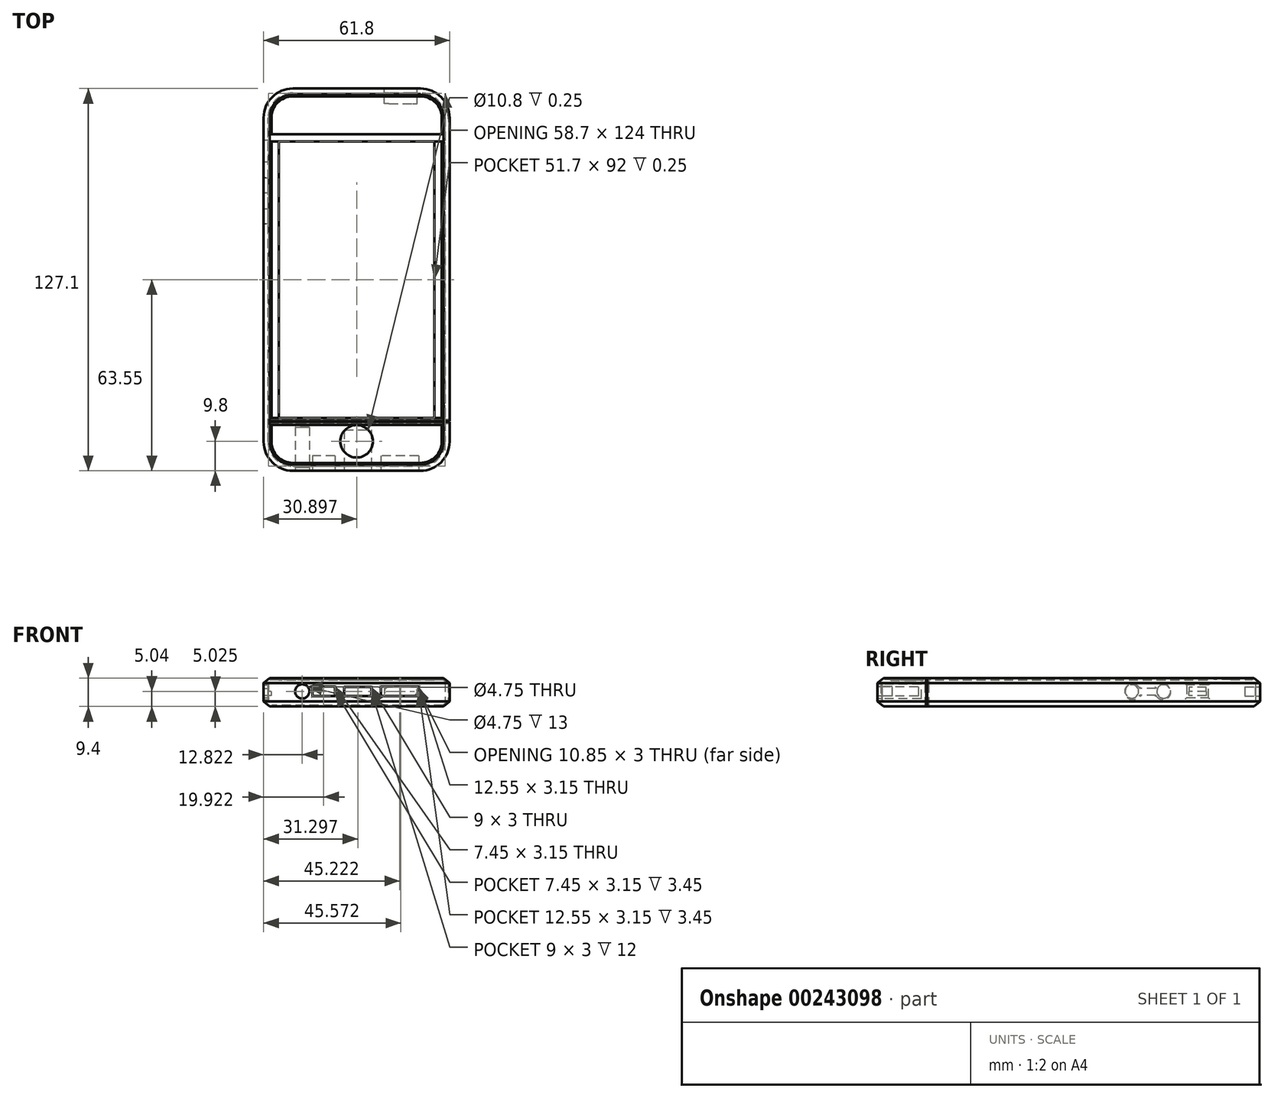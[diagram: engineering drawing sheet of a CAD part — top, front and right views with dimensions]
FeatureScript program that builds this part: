
annotation { "Feature Type Name" : "Feature", "Feature Type Description" : "" }
export const myFeature = defineFeature(function(context is Context, id is Id, definition is map)
    precondition{}
    {
        {
            var Q0;
            Q0=qCreatedBy(makeId("Top.planeOp"),FACE);
            var sketch = newSketch(context, id + "F0", { "sketchPlane" : qUnion([Q0])});
            skLineSegment(sketch, "E0.bottom", {"start": v(30.56, 124) * mm, "end": v(89.26, 124) * mm});
            skLineSegment(sketch, "E0.top", {"start": v(30.56, 0) * mm, "end": v(89.26, 0) * mm});
            skLineSegment(sketch, "E0.left", {"start": v(30.56, 124) * mm, "end": v(30.56, 0) * mm});
            skLineSegment(sketch, "E0.right", {"start": v(89.26, 124) * mm, "end": v(89.26, 0) * mm});
            skSolve(sketch);
        }
        {
            var Q0;
            Q0=makeQuery(id+"F0.imprint","IMPRINT",FACE,{"disambiguationData":[TD([[makeQuery(id+"F0.imprint","IMPRINT",EDGE,{"derivedFrom":sQuery(id+"F0.wireOp",EDGE,"E0.bottom")}),-1.0]])]});
            extrude(context, id + "F1", {"entities" : qUnion([Q0]), "depth" : 7.75 * mm});
        }
        {
            var Q0;
            Q0=makeQuery(id+"F1.opExtrude","CAP_FACE",FACE,{"disambiguationData":[OSD([sQuery(id+"F0.wireOp",EDGE,"E0.bottom"),sQuery(id+"F0.wireOp",EDGE,"E0.top"),sQuery(id+"F0.wireOp",EDGE,"E0.left"),sQuery(id+"F0.wireOp",EDGE,"E0.right")])],"isStart":false});
            var sketch = newSketch(context, id + "F2", { "sketchPlane" : qUnion([Q0])});
            skLineSegment(sketch, "E1", {"start": v(30.56, 0) * mm, "end": v(30.56, 16) * mm, "construction": true});
            skLineSegment(sketch, "E2", {"start": v(30.56, 124) * mm, "end": v(30.56, 108) * mm, "construction": true});
            skLineSegment(sketch, "E3", {"start": v(89.26, 124) * mm, "end": v(80.16, 124) * mm, "construction": true});
            skLineSegment(sketch, "E4", {"start": v(80.16, 124) * mm, "end": v(70.66, 124) * mm});
            skPoint(sketch, "E5", {"position": v(30.56, 113.5) * mm});
            skPoint(sketch, "E5.positionSnap0", {"position": v(30.56, 116) * mm});
            skLineSegment(sketch, "E6", {"start": v(89.26, 0) * mm, "end": v(89.26, 13.65) * mm, "construction": true});
            skCircle(sketch, "E7", {"center": v(59.9, 8.25) * mm, "radius": 5.4 * mm});
            skLineSegment(sketch, "E8", {"start": v(85.76, 16) * mm, "end": v(34.06, 16) * mm});
            skLineSegment(sketch, "E9", {"start": v(34.06, 16) * mm, "end": v(34.06, 108) * mm});
            skLineSegment(sketch, "E10", {"start": v(34.06, 108) * mm, "end": v(85.76, 108) * mm});
            skLineSegment(sketch, "E11", {"start": v(85.76, 108) * mm, "end": v(85.76, 16) * mm});
            skSolve(sketch);
        }
        {
            var Q0;
            Q0=makeQuery(id+"F1.opExtrude","CAP_FACE",FACE,{"disambiguationData":[OSD([sQuery(id+"F0.wireOp",EDGE,"E0.bottom"),sQuery(id+"F0.wireOp",EDGE,"E0.top"),sQuery(id+"F0.wireOp",EDGE,"E0.left"),sQuery(id+"F0.wireOp",EDGE,"E0.right")])],"isStart":true});
            var sketch = newSketch(context, id + "F3", { "sketchPlane" : qUnion([Q0])});
            skLineSegment(sketch, "E12", {"start": v(89.26, -124) * mm, "end": v(77.86, -124) * mm, "construction": true});
            skLineSegment(sketch, "E13", {"start": v(89.26, 0) * mm, "end": v(89.26, -10.45) * mm, "construction": true});
            skLineSegment(sketch, "E14", {"start": v(89.26, -10.45) * mm, "end": v(30.56, -10.45) * mm});
            skCircle(sketch, "E15", {"center": v(82.26, -116.6) * mm, "radius": 3.1 * mm});
            skCircle(sketch, "E16", {"center": v(72.23, -116.6) * mm, "radius": 1.93 * mm});
            skSolve(sketch);
        }
        {
            var Q0;
            Q0=makeQuery(id+"F1.opExtrude","SWEPT_FACE",FACE,{"disambiguationData":[OSD([sQuery(id+"F0.wireOp",EDGE,"E0.left")])]});
            var sketch = newSketch(context, id + "F4", { "sketchPlane" : qUnion([Q0])});
            skLineSegment(sketch, "E17", {"start": v(-124, 7.75) * mm, "end": v(-107.5, 7.75) * mm, "construction": true});
            skLineSegment(sketch, "E18", {"start": v(-107.5, 7.75) * mm, "end": v(-91.25, 7.75) * mm, "construction": true});
            skLineSegment(sketch, "E19", {"start": v(-91.25, 7.75) * mm, "end": v(-91.25, 0) * mm});
            skLineSegment(sketch, "E20", {"start": v(-91.25, 3.88) * mm, "end": v(-93.52, 3.88) * mm});
            skCircle(sketch, "E21", {"center": v(-93.52, 3.88) * mm, "radius": 2.27 * mm});
            skLineSegment(sketch, "E22", {"start": v(-91.25, 3.88) * mm, "end": v(-85.25, 3.88) * mm});
            skLineSegment(sketch, "E23", {"start": v(-85.25, 3.88) * mm, "end": v(-82.97, 3.88) * mm});
            skCircle(sketch, "E24", {"center": v(-82.97, 3.88) * mm, "radius": 2.27 * mm});
            skLineSegment(sketch, "E25", {"start": v(-93.52, 3.88) * mm, "end": v(-95.8, 3.88) * mm, "construction": true});
            skPoint(sketch, "E26.0", {"position": v(-124, 7.75) * mm});
            skLineSegment(sketch, "E27", {"start": v(-124, 7.75) * mm, "end": v(-101.9, 7.75) * mm, "construction": true});
            skLineSegment(sketch, "E28", {"start": v(-124, 0) * mm, "end": v(-107.7, 0) * mm, "construction": true});
            skLineSegment(sketch, "E29", {"start": v(-107.7, 3.88) * mm, "end": v(-107.7, 2.52) * mm});
            skLineSegment(sketch, "E30", {"start": v(-107.7, 2.52) * mm, "end": v(-101.9, 2.52) * mm});
            skLineSegment(sketch, "E31", {"start": v(-101.9, 2.52) * mm, "end": v(-101.9, 3.88) * mm});
            skLineSegment(sketch, "E32", {"start": v(-101.9, 3.88) * mm, "end": v(-101.9, 5.22) * mm});
            skLineSegment(sketch, "E33", {"start": v(-101.9, 5.22) * mm, "end": v(-107.7, 5.22) * mm});
            skLineSegment(sketch, "E34", {"start": v(-107.7, 5.22) * mm, "end": v(-107.7, 3.88) * mm});
            skLineSegment(sketch, "E35", {"start": v(-101.9, 3.88) * mm, "end": v(-107.7, 3.88) * mm});
            skSolve(sketch);
        }
        {
            var Q0;
            Q0=makeQuery(id+"F1.opExtrude","SWEPT_FACE",FACE,{"disambiguationData":[OSD([sQuery(id+"F0.wireOp",EDGE,"E0.top")])]});
            var sketch = newSketch(context, id + "F5", { "sketchPlane" : qUnion([Q0])});
            skLineSegment(sketch, "E36", {"start": v(89.26, 7.75) * mm, "end": v(80.5, 7.75) * mm, "construction": true});
            skLineSegment(sketch, "E37", {"start": v(80.5, 7.75) * mm, "end": v(67.96, 7.75) * mm, "construction": true});
            skLineSegment(sketch, "E38", {"start": v(89.26, 3.88) * mm, "end": v(30.56, 3.88) * mm, "construction": true});
            skLineSegment(sketch, "E39", {"start": v(80.5, 3.88) * mm, "end": v(80.5, 5.45) * mm});
            skLineSegment(sketch, "E40", {"start": v(80.5, 3.88) * mm, "end": v(80.5, 2.3) * mm});
            skLineSegment(sketch, "E41", {"start": v(80.5, 5.45) * mm, "end": v(67.96, 5.45) * mm});
            skLineSegment(sketch, "E42", {"start": v(67.96, 5.45) * mm, "end": v(67.96, 2.3) * mm});
            skLineSegment(sketch, "E43", {"start": v(67.96, 2.3) * mm, "end": v(80.5, 2.3) * mm});
            skLineSegment(sketch, "E44", {"start": v(67.96, 7.75) * mm, "end": v(64.8, 7.75) * mm, "construction": true});
            skLineSegment(sketch, "E45", {"start": v(64.8, 7.75) * mm, "end": v(55.8, 7.75) * mm, "construction": true});
            skLineSegment(sketch, "E46", {"start": v(55.8, 7.75) * mm, "end": v(52.66, 7.75) * mm, "construction": true});
            skLineSegment(sketch, "E47", {"start": v(52.66, 7.75) * mm, "end": v(45.2, 7.75) * mm, "construction": true});
            skLineSegment(sketch, "E48", {"start": v(52.66, 3.88) * mm, "end": v(52.66, 2.3) * mm, "construction": true});
            skLineSegment(sketch, "E49", {"start": v(52.66, 2.3) * mm, "end": v(45.2, 2.3) * mm});
            skLineSegment(sketch, "E50", {"start": v(45.2, 2.3) * mm, "end": v(45.2, 5.45) * mm});
            skLineSegment(sketch, "E51", {"start": v(45.2, 5.45) * mm, "end": v(52.66, 5.45) * mm});
            skLineSegment(sketch, "E52", {"start": v(52.66, 5.45) * mm, "end": v(52.66, 2.3) * mm});
            skLineSegment(sketch, "E53", {"start": v(55.8, 5.39) * mm, "end": v(64.8, 5.39) * mm});
            skLineSegment(sketch, "E54", {"start": v(64.8, 5.39) * mm, "end": v(64.8, 2.39) * mm});
            skLineSegment(sketch, "E55", {"start": v(64.8, 2.39) * mm, "end": v(55.8, 2.39) * mm});
            skLineSegment(sketch, "E56", {"start": v(55.8, 5.39) * mm, "end": v(55.8, 2.39) * mm});
            skPoint(sketch, "E57.endSnap0", {"position": v(41.83, 5.45) * mm});
            skCircle(sketch, "E58", {"center": v(41.83, 3.88) * mm, "radius": 2.37 * mm});
            skSolve(sketch);
        }
        {
            var Q0;
            Q0=makeQuery(id+"F1.opExtrude","SWEPT_EDGE",EDGE,{"disambiguationData":[OSD([sQuery(id+"F0.wireOp",EDGE,"E0.bottom"),sQuery(id+"F0.wireOp",EDGE,"E0.left")])]});
            var Q1;
            Q1=makeQuery(id+"F1.opExtrude","SWEPT_EDGE",EDGE,{"disambiguationData":[OSD([sQuery(id+"F0.wireOp",EDGE,"E0.bottom"),sQuery(id+"F0.wireOp",EDGE,"E0.right")])]});
            var Q2;
            Q2=makeQuery(id+"F1.opExtrude","SWEPT_EDGE",EDGE,{"disambiguationData":[OSD([sQuery(id+"F0.wireOp",EDGE,"E0.top"),sQuery(id+"F0.wireOp",EDGE,"E0.left")])]});
            var Q3;
            Q3=makeQuery(id+"F1.opExtrude","SWEPT_EDGE",EDGE,{"disambiguationData":[OSD([sQuery(id+"F0.wireOp",EDGE,"E0.top"),sQuery(id+"F0.wireOp",EDGE,"E0.right")])]});
            fillet(context, id + "F6", {"entities" : qUnion([Q0, Q1, Q2, Q3]), "radius" : 8.15 * mm, "tangentPropagation" : true, "allowEdgeOverflow" : false});
        }
        {
            var Q0;
            Q0=makeQuery(id+"F1.opExtrude","SWEPT_FACE",FACE,{"disambiguationData":[OSD([sQuery(id+"F0.wireOp",EDGE,"E0.bottom")])]});
            var sketch = newSketch(context, id + "F7", { "sketchPlane" : qUnion([Q0])});
            skLineSegment(sketch, "E59", {"start": v(-70.66, 0) * mm, "end": v(-80.16, 0) * mm, "construction": true});
            skArc(sketch, "E60", {"start": v(-78.5, 4.97) * mm, "mid": v(-79.6, 3.88) * mm, "end": v(-78.5, 2.78) * mm});
            skLineSegment(sketch, "E61", {"start": v(-78.5, 4.97) * mm, "end": v(-70.66, 4.98) * mm});
            skLineSegment(sketch, "E62", {"start": v(-70.66, 2.78) * mm, "end": v(-78.5, 2.78) * mm});
            skPoint(sketch, "E63.endSnap0", {"position": v(-70.66, 3.88) * mm});
            skArc(sketch, "E64", {"start": v(-70.66, 2.78) * mm, "mid": v(-69.56, 3.88) * mm, "end": v(-70.66, 4.98) * mm});
            skSolve(sketch);
        }
        {
            var Q0;
            Q0=makeQuery(id+"F5.imprint","IMPRINT",FACE,{"disambiguationData":[TD([[makeQuery(id+"F5.imprint","IMPRINT",EDGE,{"derivedFrom":sQuery(id+"F5.wireOp",EDGE,"E58")}),1.0]])]});
            extrude(context, id + "F8", {"entities" : qUnion([Q0]), "operationType" : NewBodyOperationType.REMOVE, "oppositeDirection" : true, "depth" : 13 * mm});
        }
        {
            var Q0;
            Q0=qSketchRegion(id+"F7",true);
            extrude(context, id + "F9", {"entities" : qUnion([Q0]), "operationType" : NewBodyOperationType.ADD, "depth" : .9 * mm});
        }
        {
            var Q0;
            Q0=makeQuery(id+"F4.imprint","IMPRINT",FACE,{"disambiguationData":[TD([[makeQuery(id+"F4.imprint","IMPRINT",EDGE,{"derivedFrom":sQuery(id+"F4.wireOp",EDGE,"E21")}),1.0]])]});
            var Q1;
            Q1=makeQuery(id+"F4.imprint","IMPRINT",FACE,{"disambiguationData":[TD([[makeQuery(id+"F4.imprint","IMPRINT",EDGE,{"derivedFrom":sQuery(id+"F4.wireOp",EDGE,"E24")}),1.0]])]});
            var Q2;
            Q2=makeQuery(id+"F4.imprint","IMPRINT",FACE,{"disambiguationData":[TD([[makeQuery(id+"F4.imprint","IMPRINT",EDGE,{"derivedFrom":sQuery(id+"F4.wireOp",EDGE,"E32")}),1.0]])]});
            extrude(context, id + "F10", {"entities" : qUnion([Q0, Q1, Q2]), "operationType" : NewBodyOperationType.ADD, "depth" : .9 * mm});
        }
        {
            var Q0;
            Q0=makeQuery(id+"F4.imprint","IMPRINT",FACE,{"disambiguationData":[TD([[makeQuery(id+"F4.imprint","IMPRINT",EDGE,{"derivedFrom":sQuery(id+"F4.wireOp",EDGE,"E29")}),1.0]])]});
            extrude(context, id + "F11", {"entities" : qUnion([Q0]), "operationType" : NewBodyOperationType.REMOVE, "oppositeDirection" : true, "depth" : .9 * mm});
        }
        {
            var Q0;
            Q0=makeQuery(id+"F5.imprint","IMPRINT",FACE,{"disambiguationData":[TD([[makeQuery(id+"F5.imprint","IMPRINT",EDGE,{"derivedFrom":sQuery(id+"F5.wireOp",EDGE,"E53")}),-1.0]])]});
            extrude(context, id + "F12", {"entities" : qUnion([Q0]), "operationType" : NewBodyOperationType.REMOVE, "oppositeDirection" : true, "depth" : 12 * mm});
        }
        {
            var Q0;
            Q0=makeQuery(id+"F2.imprint","IMPRINT",FACE,{"disambiguationData":[TD([[makeQuery(id+"F2.imprint","IMPRINT",EDGE,{"derivedFrom":sQuery(id+"F2.wireOp",EDGE,"E7")}),1.0]])]});
            var Q1;
            Q1=sQuery(id+"F2.wireOp",EDGE,"E7");
            extrude(context, id + "F13", {"entities" : qUnion([Q0]), "operationType" : NewBodyOperationType.REMOVE, "surfaceEntities" : qUnion([Q1]), "oppositeDirection" : true, "depth" : .25 * mm});
        }
        {
            var Q0;
            {var subQ2=sQuery(id+"F2.wireOp",EDGE,"E4");Q0=makeQuery(id+"F2.imprint","IMPRINT",FACE,{"disambiguationData":[TD([[makeQuery(id+"F2.imprint","IMPRINT",EDGE,{"derivedFrom":subQ2}),-1.0]])]});}
            var sketch = newSketch(context, id + "F14", { "sketchPlane" : qUnion([Q0])});
            skArc(sketch, "E65.0", {"start": v(81.1, 0) * mm, "mid": v(86.87, 2.39) * mm, "end": v(89.26, 8.15) * mm});
            skLineSegment(sketch, "E66.0", {"start": v(89.26, 115.85) * mm, "end": v(89.26, 8.15) * mm});
            skLineSegment(sketch, "E67.0", {"start": v(38.7, 0) * mm, "end": v(81.1, 0) * mm});
            skArc(sketch, "E68.0", {"start": v(30.56, 8.15) * mm, "mid": v(32.94, 2.39) * mm, "end": v(38.7, 0) * mm});
            skLineSegment(sketch, "E69.0", {"start": v(30.56, 115.85) * mm, "end": v(30.56, 8.15) * mm});
            skArc(sketch, "E70.0", {"start": v(38.7, 124) * mm, "mid": v(32.94, 121.61) * mm, "end": v(30.56, 115.85) * mm});
            skLineSegment(sketch, "E71.0", {"start": v(38.7, 124) * mm, "end": v(81.1, 124) * mm});
            skArc(sketch, "E72.0", {"start": v(89.26, 115.85) * mm, "mid": v(86.87, 121.61) * mm, "end": v(81.1, 124) * mm});
            skArc(sketch, "E73", {"start": v(88.2, 8.15) * mm, "mid": v(86.13, 3.13) * mm, "end": v(81.1, 1.05) * mm});
            skLineSegment(sketch, "E74", {"start": v(81.1, 1.05) * mm, "end": v(38.7, 1.05) * mm});
            skArc(sketch, "E75", {"start": v(31.6, 8.15) * mm, "mid": v(33.69, 3.13) * mm, "end": v(38.7, 1.05) * mm});
            skLineSegment(sketch, "E76", {"start": v(31.6, 8.15) * mm, "end": v(31.6, 115.85) * mm});
            skArc(sketch, "E77", {"start": v(31.6, 115.85) * mm, "mid": v(33.69, 120.87) * mm, "end": v(38.7, 122.95) * mm});
            skLineSegment(sketch, "E78", {"start": v(38.7, 122.95) * mm, "end": v(81.1, 122.95) * mm});
            skArc(sketch, "E79", {"start": v(81.1, 122.95) * mm, "mid": v(86.13, 120.87) * mm, "end": v(88.2, 115.85) * mm});
            skLineSegment(sketch, "E80", {"start": v(88.2, 115.85) * mm, "end": v(88.2, 8.15) * mm});
            skSolve(sketch);
        }
        {
            var Q0;
            Q0=qSketchRegion(id+"F14",true);
            extrude(context, id + "F15", {"entities" : qUnion([Q0]), "operationType" : NewBodyOperationType.REMOVE, "oppositeDirection" : true, "depth" : .55 * mm});
        }
        {
            var Q0;
            Q0=makeQuery(id+"F15.boolean.opBoolean","COPY",EDGE,{"derivedFrom":makeQuery(id+"F15.opExtrude","CAP_EDGE",EDGE,{"disambiguationData":[OSD([sQuery(id+"F14.wireOp",EDGE,"E71.0")])],"isStart":false})});
            var Q1;
            Q1=makeQuery(id+"F15.boolean.opBoolean","COPY",EDGE,{"derivedFrom":makeQuery(id+"F15.opExtrude","CAP_EDGE",EDGE,{"disambiguationData":[OSD([sQuery(id+"F14.wireOp",EDGE,"E72.0")])],"isStart":false})});
            var Q2;
            Q2=makeQuery(id+"F15.boolean.opBoolean","COPY",EDGE,{"derivedFrom":makeQuery(id+"F15.opExtrude","CAP_EDGE",EDGE,{"disambiguationData":[OSD([sQuery(id+"F14.wireOp",EDGE,"E66.0")])],"isStart":false})});
            var Q3;
            Q3=makeQuery(id+"F15.boolean.opBoolean","COPY",EDGE,{"derivedFrom":makeQuery(id+"F15.opExtrude","CAP_EDGE",EDGE,{"disambiguationData":[OSD([sQuery(id+"F14.wireOp",EDGE,"E65.0")])],"isStart":false})});
            var Q4;
            Q4=makeQuery(id+"F15.boolean.opBoolean","COPY",EDGE,{"derivedFrom":makeQuery(id+"F15.opExtrude","CAP_EDGE",EDGE,{"disambiguationData":[OSD([sQuery(id+"F14.wireOp",EDGE,"E67.0")])],"isStart":false})});
            var Q5;
            Q5=makeQuery(id+"F15.boolean.opBoolean","COPY",EDGE,{"derivedFrom":makeQuery(id+"F15.opExtrude","CAP_EDGE",EDGE,{"disambiguationData":[OSD([sQuery(id+"F14.wireOp",EDGE,"E68.0")])],"isStart":false})});
            var Q6;
            Q6=makeQuery(id+"F15.boolean.opBoolean","COPY",EDGE,{"derivedFrom":makeQuery(id+"F15.opExtrude","CAP_EDGE",EDGE,{"disambiguationData":[OSD([sQuery(id+"F14.wireOp",EDGE,"E69.0")])],"isStart":false})});
            var Q7;
            Q7=makeQuery(id+"F15.boolean.opBoolean","COPY",EDGE,{"derivedFrom":makeQuery(id+"F15.opExtrude","CAP_EDGE",EDGE,{"disambiguationData":[OSD([sQuery(id+"F14.wireOp",EDGE,"E70.0")])],"isStart":false})});
            var Q8;
            Q8=makeQuery(id+"F1.opExtrude","CAP_EDGE",EDGE,{"disambiguationData":[OSD([sQuery(id+"F0.wireOp",EDGE,"E0.right")])],"isStart":true});
            chamfer(context, id + "F16", {"entities" : qUnion([Q0, Q1, Q2, Q3, Q4, Q5, Q6, Q7, Q8]), "width" : .5 * mm, "tangentPropagation" : true});
        }
        {
            var Q0;
            Q0=makeQuery(id+"F2.imprint","IMPRINT",FACE,{"disambiguationData":[TD([[makeQuery(id+"F2.imprint","IMPRINT",EDGE,{"derivedFrom":sQuery(id+"F2.wireOp",EDGE,"E8")}),-1.0]])]});
            extrude(context, id + "F17", {"entities" : qUnion([Q0]), "operationType" : NewBodyOperationType.REMOVE, "oppositeDirection" : true, "depth" : .25 * mm});
        }
        {
            var Q0;
            {var subQ2=sQuery(id+"F2.wireOp",EDGE,"E4");Q0=makeQuery(id+"F2.imprint","IMPRINT",FACE,{"disambiguationData":[TD([[makeQuery(id+"F2.imprint","IMPRINT",EDGE,{"derivedFrom":subQ2}),-1.0]])]});}
            var sketch = newSketch(context, id + "F18", { "sketchPlane" : qUnion([Q0])});
            skPoint(sketch, "E81.0", {"position": v(34.06, 108) * mm});
            skLineSegment(sketch, "E82.0", {"start": v(30.56, 124) * mm, "end": v(30.56, 107.7) * mm});
            skLineSegment(sketch, "E83.0", {"start": v(31.06, 115.85) * mm, "end": v(31.06, 8.15) * mm});
            skLineSegment(sketch, "E84.0", {"start": v(31.6, 8.15) * mm, "end": v(31.6, 115.85) * mm});
            skLineSegment(sketch, "E85", {"start": v(31.06, 108) * mm, "end": v(30.56, 108) * mm});
            skLineSegment(sketch, "E86", {"start": v(34.06, 108) * mm, "end": v(31.6, 108) * mm});
            skLineSegment(sketch, "E87", {"start": v(31.06, 108) * mm, "end": v(31.6, 108) * mm});
            skLineSegment(sketch, "E88", {"start": v(30.56, 108) * mm, "end": v(30.56, 124) * mm});
            skSolve(sketch);
        }
        {
            var Q0;
            Q0=makeQuery(id+"F1.opExtrude","SWEPT_FACE",FACE,{"disambiguationData":[OSD([sQuery(id+"F0.wireOp",EDGE,"E0.bottom")])]});
            cPlane(context, id + "F19", {"entities" : qUnion([Q0]), "cplaneType" : CPlaneType.OFFSET, "offset" : 8.5 * mm, "oppositeDirection" : true, "width" : 150 * mm, "height" : 150 * mm});
        }
        {
            var Q0;
            {var subQ5=sQuery(id+"F4.wireOp",EDGE,"E21");Q0=makeQuery(id+"F4.imprint","IMPRINT",FACE,{"disambiguationData":[TD([[makeQuery(id+"F4.imprint","IMPRINT",EDGE,{"derivedFrom":subQ5}),-1.0]])]});}
            var sketch = newSketch(context, id + "F20", { "sketchPlane" : qUnion([Q0])});
            skLineSegment(sketch, "E89.0", {"start": v(-8.15, 7.75) * mm, "end": v(-115.85, 7.75) * mm});
            skLineSegment(sketch, "E90.0", {"start": v(-115.85, 7.2) * mm, "end": v(-8.15, 7.2) * mm});
            skLineSegment(sketch, "E91.0", {"start": v(-8.15, 6.7) * mm, "end": v(-115.85, 6.7) * mm});
            skLineSegment(sketch, "E92.0", {"start": v(-115.85, 0.5) * mm, "end": v(-8.15, 0.5) * mm});
            skLineSegment(sketch, "E93.0", {"start": v(-8.15, 0) * mm, "end": v(-115.85, 0) * mm});
            skPoint(sketch, "E94.0", {"position": v(-108, 7.75) * mm});
            skLineSegment(sketch, "E95", {"start": v(-108, 7.75) * mm, "end": v(-108, 7.2) * mm});
            skLineSegment(sketch, "E96", {"start": v(-108, 7.2) * mm, "end": v(-108, 6.7) * mm});
            skLineSegment(sketch, "E97", {"start": v(-108, 6.7) * mm, "end": v(-108, 0.5) * mm});
            skLineSegment(sketch, "E98", {"start": v(-108, 0.5) * mm, "end": v(-108, 0) * mm});
            skSolve(sketch);
        }
        {
            var Q0;
            Q0=qCreatedBy(id+"F19.planeOp",FACE);
            var sketch = newSketch(context, id + "F21", { "sketchPlane" : qUnion([Q0])});
            skPoint(sketch, "E99.0", {"position": v(-34.06, 7.75) * mm});
            skPoint(sketch, "E100.0", {"position": v(-31.6, 7.75) * mm});
            skPoint(sketch, "E101.0", {"position": v(-31.06, 7.75) * mm});
            skPoint(sketch, "E102.0", {"position": v(-30.56, 7.75) * mm});
            skPoint(sketch, "E103.0", {"position": v(-30.56, 7.2) * mm});
            skPoint(sketch, "E104.0", {"position": v(-30.56, 6.7) * mm});
            skPoint(sketch, "E105.0", {"position": v(-30.56, 0.5) * mm});
            skPoint(sketch, "E106.0", {"position": v(-30.56, 0) * mm});
            skLineSegment(sketch, "E107", {"start": v(-31.6, 7.2) * mm, "end": v(-31.6, 7.75) * mm});
            skLineSegment(sketch, "E108", {"start": v(-31.06, 7.2) * mm, "end": v(-30.56, 6.7) * mm});
            skLineSegment(sketch, "E109", {"start": v(-31.06, 0) * mm, "end": v(-30.56, 0.5) * mm});
            skLineSegment(sketch, "E110", {"start": v(-31.6, 7.2) * mm, "end": v(-31.06, 7.2) * mm});
            skLineSegment(sketch, "E111", {"start": v(-30.56, 6.7) * mm, "end": v(-30.5, 6.7) * mm});
            skLineSegment(sketch, "E112", {"start": v(-30.5, 6.7) * mm, "end": v(-30.53, 0.5) * mm});
            skPoint(sketch, "E112.endSnap0", {"position": v(-30.53, 6.7) * mm});
            skLineSegment(sketch, "E113", {"start": v(-30.53, 0.5) * mm, "end": v(-30.56, 0.5) * mm});
            skLineSegment(sketch, "E114", {"start": v(-31.06, 7.75) * mm, "end": v(-31.06, 8.25) * mm});
            skLineSegment(sketch, "E115", {"start": v(-31.6, 7.75) * mm, "end": v(-31.06, 8.25) * mm});
            skLineSegment(sketch, "E116", {"start": v(-31.06, 8.25) * mm, "end": v(-29, 6.7) * mm});
            skLineSegment(sketch, "E117", {"start": v(-29, 6.7) * mm, "end": v(-29, 0.5) * mm});
            skLineSegment(sketch, "E118", {"start": v(-31.06, 0) * mm, "end": v(-31.06, -1.15) * mm});
            skLineSegment(sketch, "E119", {"start": v(-31.06, -1.15) * mm, "end": v(-29, 0.5) * mm});
            skLineSegment(sketch, "E120", {"start": v(-29, 6.7) * mm, "end": v(-30.5, 6.7) * mm, "construction": true});
            skSolve(sketch);
        }
        {
            var Q0;
            {var subQ2=sQuery(id+"F2.wireOp",EDGE,"E4");Q0=makeQuery(id+"F2.imprint","IMPRINT",FACE,{"disambiguationData":[TD([[makeQuery(id+"F2.imprint","IMPRINT",EDGE,{"derivedFrom":subQ2}),-1.0]])]});}
            var sketch = newSketch(context, id + "F22", { "sketchPlane" : qUnion([Q0])});
            skPoint(sketch, "E121.0", {"position": v(31.6, 115.85) * mm});
            skArc(sketch, "E122.0", {"start": v(31.6, 115.85) * mm, "mid": v(33.69, 120.87) * mm, "end": v(38.7, 122.95) * mm});
            skLineSegment(sketch, "E123.0", {"start": v(38.7, 122.95) * mm, "end": v(81.1, 122.95) * mm});
            skArc(sketch, "E124.0", {"start": v(81.1, 122.95) * mm, "mid": v(86.13, 120.87) * mm, "end": v(88.2, 115.85) * mm});
            skLineSegment(sketch, "E125.0", {"start": v(88.2, 115.85) * mm, "end": v(88.2, 8.15) * mm});
            skArc(sketch, "E126.0", {"start": v(88.2, 8.15) * mm, "mid": v(86.13, 3.13) * mm, "end": v(81.1, 1.05) * mm});
            skLineSegment(sketch, "E127.0", {"start": v(81.1, 1.05) * mm, "end": v(38.7, 1.05) * mm});
            skArc(sketch, "E128.0", {"start": v(31.6, 8.15) * mm, "mid": v(33.69, 3.13) * mm, "end": v(38.7, 1.05) * mm});
            skSolve(sketch);
        }
        {
            var Q0;
            Q0 = qSketchRegion(id + "F21", true);
            var Q1;
            Q1=sQuery(id+"F22.wireOp",EDGE,"E122.0");
            var Q2;
            Q2=sQuery(id+"F22.wireOp",EDGE,"E123.0");
            var Q3;
            Q3=sQuery(id+"F22.wireOp",EDGE,"E124.0");
            var Q4;
            Q4=sQuery(id+"F22.wireOp",EDGE,"E125.0");
            var Q5;
            Q5=sQuery(id+"F22.wireOp",EDGE,"E126.0");
            var Q6;
            Q6=sQuery(id+"F22.wireOp",EDGE,"E127.0");
            var Q7;
            Q7=sQuery(id+"F14.wireOp",EDGE,"E75");
            var Q8;
            Q8=sQuery(id+"F18.wireOp",EDGE,"E84.0");
            sweep(context, id + "F23", {"profiles" : qUnion([Q0]), "path" : qUnion([Q1, Q2, Q3, Q4, Q5, Q6, Q7, Q8])});
        }
        {
            var Q0;
            Q0=makeQuery(id+"F23.opSweep","SWEPT_FACE",FACE,{"disambiguationData":[OSD([sQuery(id+"F21.wireOp",EDGE,"E117"),sQuery(id+"F22.wireOp",EDGE,"E127.0")])]});
            var sketch = newSketch(context, id + "F24", { "sketchPlane" : qUnion([Q0])});
            skCircle(sketch, "E129.0", {"center": v(41.83, 3.88) * mm, "radius": 2.37 * mm});
            skLineSegment(sketch, "E130.0", {"start": v(45.2, 5.45) * mm, "end": v(52.66, 5.45) * mm});
            skLineSegment(sketch, "E131.0", {"start": v(52.66, 2.3) * mm, "end": v(45.2, 2.3) * mm});
            skPoint(sketch, "E132.0", {"position": v(45.2, 3.87) * mm});
            skLineSegment(sketch, "E133.0", {"start": v(45.2, 2.3) * mm, "end": v(45.2, 5.45) * mm});
            skLineSegment(sketch, "E134.0", {"start": v(52.66, 5.45) * mm, "end": v(52.66, 2.3) * mm});
            skLineSegment(sketch, "E135.0", {"start": v(55.8, 5.39) * mm, "end": v(55.8, 2.39) * mm});
            skLineSegment(sketch, "E136.0", {"start": v(55.8, 5.39) * mm, "end": v(64.8, 5.39) * mm});
            skLineSegment(sketch, "E137.0", {"start": v(64.8, 2.39) * mm, "end": v(55.8, 2.39) * mm});
            skLineSegment(sketch, "E138.0", {"start": v(64.8, 5.39) * mm, "end": v(64.8, 2.39) * mm});
            skLineSegment(sketch, "E139.0", {"start": v(80.5, 5.45) * mm, "end": v(67.96, 5.45) * mm});
            skLineSegment(sketch, "E140.0", {"start": v(67.96, 5.45) * mm, "end": v(67.96, 2.3) * mm});
            skLineSegment(sketch, "E141.0", {"start": v(67.96, 2.3) * mm, "end": v(80.5, 2.3) * mm});
            skLineSegment(sketch, "E142.0", {"start": v(80.5, 3.88) * mm, "end": v(80.5, 5.45) * mm});
            skLineSegment(sketch, "E143.0", {"start": v(80.5, 3.88) * mm, "end": v(80.5, 2.3) * mm});
            skSolve(sketch);
        }
        {
            var Q0;
            Q0 = qSketchRegion(id + "F24", true);
            extrude(context, id + "F25", {"entities" : qUnion([Q0]), "operationType" : NewBodyOperationType.REMOVE, "oppositeDirection" : true, "depth" : 5 * mm});
        }
        {
            var Q0;
            Q0=makeQuery(id+"F23.opSweep","SWEPT_FACE",FACE,{"disambiguationData":[OSD([sQuery(id+"F18.wireOp",EDGE,"E84.0"),sQuery(id+"F21.wireOp",EDGE,"E117")])]});
            cPlane(context, id + "F26", {"entities" : qUnion([Q0]), "cplaneType" : CPlaneType.OFFSET, "offset" : 1.5 * mm, "oppositeDirection" : true, "width" : 150 * mm, "height" : 150 * mm});
        }
        {
            var Q0;
            Q0=qCreatedBy(id+"F26.planeOp",FACE);
            var sketch = newSketch(context, id + "F27", { "sketchPlane" : qUnion([Q0])});
            skPoint(sketch, "E144.0", {"position": v(-101.9, 2.52) * mm});
            skPoint(sketch, "E145.0", {"position": v(-101.9, 5.22) * mm});
            skPoint(sketch, "E146.0", {"position": v(-107.7, 5.22) * mm});
            skPoint(sketch, "E147.0", {"position": v(-107.7, 2.52) * mm});
            skCircle(sketch, "E148", {"center": v(-93.3, 3.77) * mm, "radius": 2.62 * mm});
            skCircle(sketch, "E149", {"center": v(-83.2, 3.77) * mm, "radius": 2.62 * mm});
            skLineSegment(sketch, "E150", {"start": v(-88.25, 2.63) * mm, "end": v(-90.94, 2.63) * mm});
            skLineSegment(sketch, "E151", {"start": v(-90.94, 2.63) * mm, "end": v(-85.56, 2.63) * mm});
            skLineSegment(sketch, "E152", {"start": v(-85.56, 4.9) * mm, "end": v(-90.94, 4.9) * mm});
            skPoint(sketch, "E153", {"position": v(-101.15, 1.77) * mm});
            skPoint(sketch, "E154", {"position": v(-101.15, 5.97) * mm});
            skPoint(sketch, "E155", {"position": v(-108.45, 5.97) * mm});
            skPoint(sketch, "E156", {"position": v(-108.45, 1.77) * mm});
            skLineSegment(sketch, "E157", {"start": v(-101.15, 1.77) * mm, "end": v(-101.15, 5.97) * mm});
            skLineSegment(sketch, "E158", {"start": v(-108.45, 5.97) * mm, "end": v(-108.45, 1.77) * mm});
            skLineSegment(sketch, "E159", {"start": v(-108.45, 1.77) * mm, "end": v(-101.15, 1.77) * mm});
            skLineSegment(sketch, "E160", {"start": v(-101.15, 5.97) * mm, "end": v(-108.45, 5.97) * mm});
            skSolve(sketch);
        }
        {
            var Q0;
            Q0 = qSketchRegion(id + "F27", true);
            extrude(context, id + "F28", {"entities" : qUnion([Q0]), "operationType" : NewBodyOperationType.REMOVE, "depth" : 5 * mm});
        }
        {
            var Q0;
            Q0=makeQuery(id+"F25.boolean.opBoolean","COPY",EDGE,{"derivedFrom":makeQuery(id+"F25.opExtrude","CAP_EDGE",EDGE,{"disambiguationData":[OSD([sQuery(id+"F24.wireOp",EDGE,"E129.0")])],"isStart":true})});
            var Q1;
            Q1=makeQuery(id+"F25.boolean.opBoolean","INTERSECT",EDGE,{"derivedFrom":[makeQuery(id+"F23.opSweep","SWEPT_FACE",FACE,{"disambiguationData":[OSD([sQuery(id+"F21.wireOp",EDGE,"E112"),sQuery(id+"F22.wireOp",EDGE,"E127.0")])]}),makeQuery(id+"F25.opExtrude","SWEPT_FACE",FACE,{"disambiguationData":[OSD([sQuery(id+"F24.wireOp",EDGE,"E129.0")])]})]});
            var Q2;
            Q2=makeQuery(id+"F25.boolean.opBoolean","COPY",EDGE,{"derivedFrom":makeQuery(id+"F25.opExtrude","CAP_EDGE",EDGE,{"disambiguationData":[OSD([sQuery(id+"F24.wireOp",EDGE,"E131.0")])],"isStart":true})});
            var Q3;
            Q3=makeQuery(id+"F25.boolean.opBoolean","COPY",EDGE,{"derivedFrom":makeQuery(id+"F25.opExtrude","CAP_EDGE",EDGE,{"disambiguationData":[OSD([sQuery(id+"F24.wireOp",EDGE,"E133.0")])],"isStart":true})});
            var Q4;
            Q4=makeQuery(id+"F25.boolean.opBoolean","INTERSECT",EDGE,{"derivedFrom":[makeQuery(id+"F23.opSweep","SWEPT_FACE",FACE,{"disambiguationData":[OSD([sQuery(id+"F21.wireOp",EDGE,"E112"),sQuery(id+"F22.wireOp",EDGE,"E127.0")])]}),makeQuery(id+"F25.opExtrude","SWEPT_FACE",FACE,{"disambiguationData":[OSD([sQuery(id+"F24.wireOp",EDGE,"E131.0")])]})]});
            var Q5;
            Q5=makeQuery(id+"F25.boolean.opBoolean","INTERSECT",EDGE,{"derivedFrom":[makeQuery(id+"F23.opSweep","SWEPT_FACE",FACE,{"disambiguationData":[OSD([sQuery(id+"F21.wireOp",EDGE,"E112"),sQuery(id+"F22.wireOp",EDGE,"E127.0")])]}),makeQuery(id+"F25.opExtrude","SWEPT_FACE",FACE,{"disambiguationData":[OSD([sQuery(id+"F24.wireOp",EDGE,"E133.0")])]})]});
            var Q6;
            Q6=makeQuery(id+"F25.boolean.opBoolean","COPY",EDGE,{"derivedFrom":makeQuery(id+"F25.opExtrude","CAP_EDGE",EDGE,{"disambiguationData":[OSD([sQuery(id+"F24.wireOp",EDGE,"E130.0")])],"isStart":true})});
            var Q7;
            Q7=makeQuery(id+"F25.boolean.opBoolean","INTERSECT",EDGE,{"derivedFrom":[makeQuery(id+"F23.opSweep","SWEPT_FACE",FACE,{"disambiguationData":[OSD([sQuery(id+"F21.wireOp",EDGE,"E112"),sQuery(id+"F22.wireOp",EDGE,"E127.0")])]}),makeQuery(id+"F25.opExtrude","SWEPT_FACE",FACE,{"disambiguationData":[OSD([sQuery(id+"F24.wireOp",EDGE,"E130.0")])]})]});
            var Q8;
            Q8=makeQuery(id+"F25.boolean.opBoolean","COPY",EDGE,{"derivedFrom":makeQuery(id+"F25.opExtrude","CAP_EDGE",EDGE,{"disambiguationData":[OSD([sQuery(id+"F24.wireOp",EDGE,"E134.0")])],"isStart":true})});
            var Q9;
            Q9=makeQuery(id+"F25.boolean.opBoolean","INTERSECT",EDGE,{"derivedFrom":[makeQuery(id+"F23.opSweep","SWEPT_FACE",FACE,{"disambiguationData":[OSD([sQuery(id+"F21.wireOp",EDGE,"E112"),sQuery(id+"F22.wireOp",EDGE,"E127.0")])]}),makeQuery(id+"F25.opExtrude","SWEPT_FACE",FACE,{"disambiguationData":[OSD([sQuery(id+"F24.wireOp",EDGE,"E134.0")])]})]});
            var Q10;
            Q10=makeQuery(id+"F25.boolean.opBoolean","COPY",EDGE,{"derivedFrom":makeQuery(id+"F25.opExtrude","CAP_EDGE",EDGE,{"disambiguationData":[OSD([sQuery(id+"F24.wireOp",EDGE,"E136.0")])],"isStart":true})});
            var Q11;
            Q11=makeQuery(id+"F25.boolean.opBoolean","INTERSECT",EDGE,{"derivedFrom":[makeQuery(id+"F23.opSweep","SWEPT_FACE",FACE,{"disambiguationData":[OSD([sQuery(id+"F21.wireOp",EDGE,"E112"),sQuery(id+"F22.wireOp",EDGE,"E127.0")])]}),makeQuery(id+"F25.opExtrude","SWEPT_FACE",FACE,{"disambiguationData":[OSD([sQuery(id+"F24.wireOp",EDGE,"E136.0")])]})]});
            var Q12;
            Q12=makeQuery(id+"F25.boolean.opBoolean","COPY",EDGE,{"derivedFrom":makeQuery(id+"F25.opExtrude","CAP_EDGE",EDGE,{"disambiguationData":[OSD([sQuery(id+"F24.wireOp",EDGE,"E135.0")])],"isStart":true})});
            var Q13;
            Q13=makeQuery(id+"F25.boolean.opBoolean","INTERSECT",EDGE,{"derivedFrom":[makeQuery(id+"F23.opSweep","SWEPT_FACE",FACE,{"disambiguationData":[OSD([sQuery(id+"F21.wireOp",EDGE,"E112"),sQuery(id+"F22.wireOp",EDGE,"E127.0")])]}),makeQuery(id+"F25.opExtrude","SWEPT_FACE",FACE,{"disambiguationData":[OSD([sQuery(id+"F24.wireOp",EDGE,"E138.0")])]})]});
            var Q14;
            Q14=makeQuery(id+"F25.boolean.opBoolean","COPY",EDGE,{"derivedFrom":makeQuery(id+"F25.opExtrude","CAP_EDGE",EDGE,{"disambiguationData":[OSD([sQuery(id+"F24.wireOp",EDGE,"E138.0")])],"isStart":true})});
            var Q15;
            Q15=makeQuery(id+"F12.boolean.opBoolean","COPY",EDGE,{"derivedFrom":makeQuery(id+"F12.opExtrude","CAP_EDGE",EDGE,{"disambiguationData":[OSD([sQuery(id+"F5.wireOp",EDGE,"E55")])],"isStart":true})});
            var Q16;
            Q16=makeQuery(id+"F25.boolean.opBoolean","COPY",EDGE,{"derivedFrom":makeQuery(id+"F25.opExtrude","CAP_EDGE",EDGE,{"disambiguationData":[OSD([sQuery(id+"F24.wireOp",EDGE,"E137.0")])],"isStart":true})});
            var Q17;
            Q17=makeQuery(id+"F12.boolean.opBoolean","COPY",EDGE,{"derivedFrom":makeQuery(id+"F12.opExtrude","CAP_EDGE",EDGE,{"disambiguationData":[OSD([sQuery(id+"F5.wireOp",EDGE,"E56")])],"isStart":true})});
            var Q18;
            Q18=makeQuery(id+"F25.boolean.opBoolean","COPY",EDGE,{"derivedFrom":makeQuery(id+"F25.opExtrude","CAP_EDGE",EDGE,{"disambiguationData":[OSD([sQuery(id+"F24.wireOp",EDGE,"E140.0")])],"isStart":true})});
            var Q19;
            Q19=makeQuery(id+"F25.boolean.opBoolean","INTERSECT",EDGE,{"derivedFrom":[makeQuery(id+"F23.opSweep","SWEPT_FACE",FACE,{"disambiguationData":[OSD([sQuery(id+"F21.wireOp",EDGE,"E112"),sQuery(id+"F22.wireOp",EDGE,"E127.0")])]}),makeQuery(id+"F25.opExtrude","SWEPT_FACE",FACE,{"disambiguationData":[OSD([sQuery(id+"F24.wireOp",EDGE,"E140.0")])]})]});
            var Q20;
            Q20=makeQuery(id+"F25.boolean.opBoolean","COPY",EDGE,{"derivedFrom":makeQuery(id+"F25.opExtrude","CAP_EDGE",EDGE,{"disambiguationData":[OSD([sQuery(id+"F24.wireOp",EDGE,"E139.0")])],"isStart":true})});
            var Q21;
            Q21=makeQuery(id+"F25.boolean.opBoolean","COPY",EDGE,{"derivedFrom":makeQuery(id+"F25.opExtrude","CAP_EDGE",EDGE,{"disambiguationData":[OSD([sQuery(id+"F24.wireOp",EDGE,"E141.0")])],"isStart":true})});
            var Q22;
            Q22=makeQuery(id+"F25.boolean.opBoolean","INTERSECT",EDGE,{"derivedFrom":[makeQuery(id+"F23.opSweep","SWEPT_FACE",FACE,{"disambiguationData":[OSD([sQuery(id+"F21.wireOp",EDGE,"E112"),sQuery(id+"F22.wireOp",EDGE,"E127.0")])]}),makeQuery(id+"F25.opExtrude","SWEPT_FACE",FACE,{"disambiguationData":[OSD([sQuery(id+"F24.wireOp",EDGE,"E141.0")])]})]});
            var Q23;
            Q23=makeQuery(id+"F25.boolean.opBoolean","INTERSECT",EDGE,{"derivedFrom":[makeQuery(id+"F23.opSweep","SWEPT_FACE",FACE,{"disambiguationData":[OSD([sQuery(id+"F21.wireOp",EDGE,"E112"),sQuery(id+"F22.wireOp",EDGE,"E127.0")])]}),makeQuery(id+"F25.opExtrude","SWEPT_FACE",FACE,{"disambiguationData":[OSD([sQuery(id+"F24.wireOp",EDGE,"E142.0"),sQuery(id+"F24.wireOp",EDGE,"E143.0")])]})]});
            var Q24;
            Q24=makeQuery(id+"F25.boolean.opBoolean","COPY",EDGE,{"derivedFrom":makeQuery(id+"F25.opExtrude","CAP_EDGE",EDGE,{"disambiguationData":[OSD([sQuery(id+"F24.wireOp",EDGE,"E142.0"),sQuery(id+"F24.wireOp",EDGE,"E143.0")])],"isStart":true})});
            var Q25;
            Q25=makeQuery(id+"F25.boolean.opBoolean","INTERSECT",EDGE,{"derivedFrom":[makeQuery(id+"F23.opSweep","SWEPT_FACE",FACE,{"disambiguationData":[OSD([sQuery(id+"F21.wireOp",EDGE,"E112"),sQuery(id+"F22.wireOp",EDGE,"E127.0")])]}),makeQuery(id+"F25.opExtrude","SWEPT_FACE",FACE,{"disambiguationData":[OSD([sQuery(id+"F24.wireOp",EDGE,"E139.0")])]})]});
            var Q26;
            Q26=makeQuery(id+"F28.boolean.opBoolean","INTERSECT",EDGE,{"derivedFrom":[makeQuery(id+"F23.opSweep","SWEPT_FACE",FACE,{"disambiguationData":[OSD([sQuery(id+"F18.wireOp",EDGE,"E84.0"),sQuery(id+"F21.wireOp",EDGE,"E117")])]}),makeQuery(id+"F28.opExtrude","SWEPT_FACE",FACE,{"disambiguationData":[OSD([sQuery(id+"F27.wireOp",EDGE,"E149")])]})]});
            var Q27;
            Q27=makeQuery(id+"F28.boolean.opBoolean","INTERSECT",EDGE,{"derivedFrom":[makeQuery(id+"F23.opSweep","SWEPT_FACE",FACE,{"disambiguationData":[OSD([sQuery(id+"F18.wireOp",EDGE,"E84.0"),sQuery(id+"F21.wireOp",EDGE,"E117")])]}),makeQuery(id+"F28.opExtrude","SWEPT_FACE",FACE,{"disambiguationData":[OSD([sQuery(id+"F27.wireOp",EDGE,"E152")])]})]});
            var Q28;
            Q28=makeQuery(id+"F28.boolean.opBoolean","INTERSECT",EDGE,{"derivedFrom":[makeQuery(id+"F23.opSweep","SWEPT_FACE",FACE,{"disambiguationData":[OSD([sQuery(id+"F18.wireOp",EDGE,"E84.0"),sQuery(id+"F21.wireOp",EDGE,"E117")])]}),makeQuery(id+"F28.opExtrude","SWEPT_FACE",FACE,{"disambiguationData":[OSD([sQuery(id+"F27.wireOp",EDGE,"E151")])]})]});
            var Q29;
            Q29=makeQuery(id+"F28.boolean.opBoolean","INTERSECT",EDGE,{"derivedFrom":[makeQuery(id+"F23.opSweep","SWEPT_FACE",FACE,{"disambiguationData":[OSD([sQuery(id+"F18.wireOp",EDGE,"E84.0"),sQuery(id+"F21.wireOp",EDGE,"E117")])]}),makeQuery(id+"F28.opExtrude","SWEPT_FACE",FACE,{"disambiguationData":[OSD([sQuery(id+"F27.wireOp",EDGE,"E148")])]})]});
            var Q30;
            Q30=makeQuery(id+"F28.boolean.opBoolean","INTERSECT",EDGE,{"derivedFrom":[makeQuery(id+"F23.opSweep","SWEPT_FACE",FACE,{"disambiguationData":[OSD([sQuery(id+"F18.wireOp",EDGE,"E84.0"),sQuery(id+"F21.wireOp",EDGE,"E117")])]}),makeQuery(id+"F28.opExtrude","SWEPT_FACE",FACE,{"disambiguationData":[OSD([sQuery(id+"F27.wireOp",EDGE,"E159")])]})]});
            var Q31;
            Q31=makeQuery(id+"F28.boolean.opBoolean","INTERSECT",EDGE,{"derivedFrom":[makeQuery(id+"F23.opSweep","SWEPT_FACE",FACE,{"disambiguationData":[OSD([sQuery(id+"F18.wireOp",EDGE,"E84.0"),sQuery(id+"F21.wireOp",EDGE,"E117")])]}),makeQuery(id+"F28.opExtrude","SWEPT_FACE",FACE,{"disambiguationData":[OSD([sQuery(id+"F27.wireOp",EDGE,"E157")])]})]});
            var Q32;
            Q32=makeQuery(id+"F28.boolean.opBoolean","INTERSECT",EDGE,{"derivedFrom":[makeQuery(id+"F23.opSweep","SWEPT_FACE",FACE,{"disambiguationData":[OSD([sQuery(id+"F18.wireOp",EDGE,"E84.0"),sQuery(id+"F21.wireOp",EDGE,"E117")])]}),makeQuery(id+"F28.opExtrude","SWEPT_FACE",FACE,{"disambiguationData":[OSD([sQuery(id+"F27.wireOp",EDGE,"E158")])]})]});
            var Q33;
            Q33=makeQuery(id+"F28.boolean.opBoolean","INTERSECT",EDGE,{"derivedFrom":[makeQuery(id+"F23.opSweep","SWEPT_FACE",FACE,{"disambiguationData":[OSD([sQuery(id+"F18.wireOp",EDGE,"E84.0"),sQuery(id+"F21.wireOp",EDGE,"E117")])]}),makeQuery(id+"F28.opExtrude","SWEPT_FACE",FACE,{"disambiguationData":[OSD([sQuery(id+"F27.wireOp",EDGE,"E160")])]})]});
            fillet(context, id + "F29", {"entities" : qUnion([Q0, Q1, Q2, Q3, Q4, Q5, Q6, Q7, Q8, Q9, Q10, Q11, Q12, Q13, Q14, Q15, Q16, Q17, Q18, Q19, Q20, Q21, Q22, Q23, Q24, Q25, Q26, Q27, Q28, Q29, Q30, Q31, Q32, Q33]), "radius" : .4 * mm, "tangentPropagation" : true, "allowEdgeOverflow" : false});
        }
        {
            var Q0;
            Q0=makeQuery(id+"F14.imprint","IMPRINT",FACE,{"disambiguationData":[TD([[makeQuery(id+"F14.imprint","IMPRINT",EDGE,{"derivedFrom":sQuery(id+"F14.wireOp",EDGE,"E73")}),-1.0]])]});
            var sketch = newSketch(context, id + "F30", { "sketchPlane" : qUnion([Q0])});
            skLineSegment(sketch, "E161.0", {"start": v(85.76, 16) * mm, "end": v(34.06, 16) * mm});
            skLineSegment(sketch, "E162.0", {"start": v(34.06, 108) * mm, "end": v(85.76, 108) * mm});
            skPoint(sketch, "E163", {"position": v(88.76, 16) * mm});
            skPoint(sketch, "E164", {"position": v(88.76, 13.65) * mm});
            skPoint(sketch, "E165", {"position": v(31.06, 16) * mm});
            skPoint(sketch, "E166", {"position": v(31.06, 13.65) * mm});
            skPoint(sketch, "E167", {"position": v(31.06, 110.35) * mm});
            skPoint(sketch, "E168", {"position": v(31.06, 108) * mm});
            skPoint(sketch, "E169", {"position": v(88.76, 110.35) * mm});
            skPoint(sketch, "E170", {"position": v(88.76, 108) * mm});
            skLineSegment(sketch, "E171", {"start": v(88.76, 110.35) * mm, "end": v(88.76, 108) * mm});
            skLineSegment(sketch, "E172", {"start": v(31.06, 110.35) * mm, "end": v(31.06, 108) * mm});
            skLineSegment(sketch, "E173", {"start": v(31.06, 108) * mm, "end": v(88.76, 108) * mm});
            skLineSegment(sketch, "E174", {"start": v(88.76, 110.35) * mm, "end": v(31.06, 110.35) * mm});
            skLineSegment(sketch, "E175", {"start": v(88.76, 16) * mm, "end": v(88.76, 13.65) * mm});
            skLineSegment(sketch, "E176", {"start": v(88.76, 13.65) * mm, "end": v(31.06, 13.65) * mm});
            skLineSegment(sketch, "E177", {"start": v(31.06, 13.65) * mm, "end": v(31.06, 16) * mm});
            skLineSegment(sketch, "E178", {"start": v(31.06, 16) * mm, "end": v(88.76, 16) * mm});
            skSolve(sketch);
        }
        {
            var Q0;
            Q0 = qSketchRegion(id + "F30", true);
            extrude(context, id + "F31", {"entities" : qUnion([Q0]), "operationType" : NewBodyOperationType.ADD, "depth" : .5 * mm});
        }
        {
            var Q0;
            Q0=makeQuery(id+"F31.boolean.opBoolean","MERGE",EDGE,{"derivedFrom":[makeQuery(id+"F23.opSweep","SWEPT_EDGE",EDGE,{"disambiguationData":[OSD([sQuery(id+"F18.wireOp",EDGE,"E84.0"),sQuery(id+"F21.wireOp",EDGE,"E115"),sQuery(id+"F21.wireOp",EDGE,"E116")])]}),makeQuery(id+"F31.opExtrude","CAP_EDGE",EDGE,{"disambiguationData":[OSD([sQuery(id+"F30.wireOp",EDGE,"E177")])],"isStart":false})]});
            cPoint(context, id + "F32", {"entities" : qUnion([Q0]), "parameter" : 0.5});
        }
        {
            var Q0;
            Q0=sQuery(id+"F18.wireOp",EDGE,"E83.0");
            cPoint(context, id + "F33", {"entities" : qUnion([Q0]), "parameter" : 0.5});
        }
        {
            var Q0;
            Q0 = qCreatedBy(id + "F32" ,VERTEX);
            var Q1;
            Q1=sQuery(id+"F18.wireOp",VERTEX,"E83.0.end");
            var Q2;
            Q2 = qCreatedBy(id + "F33" ,VERTEX);
            cPlane(context, id + "F34", {"entities" : qUnion([Q0, Q1, Q2]), "cplaneType" : CPlaneType.THREE_POINT, "offset" : 25 * mm, "width" : 150 * mm, "height" : 150 * mm});
        }
        {
            var Q0;
            Q0=qCreatedBy(id+"F34.planeOp",FACE);
            var sketch = newSketch(context, id + "F35", { "sketchPlane" : qUnion([Q0])});
            skPoint(sketch, "E179.0", {"position": v(-8.15, 7.75) * mm});
            skPoint(sketch, "E180.0", {"position": v(-16, 7.75) * mm});
            skPoint(sketch, "E181.endSnap0", {"position": v(-13.65, 8) * mm});
            skLineSegment(sketch, "E182", {"start": v(-14.98, 8.25) * mm, "end": v(-14.98, 8) * mm});
            skLineSegment(sketch, "E183", {"start": v(-14.98, 8) * mm, "end": v(-15.49, 8) * mm});
            skLineSegment(sketch, "E184", {"start": v(-15.49, 8) * mm, "end": v(-15.49, 7.82) * mm});
            skLineSegment(sketch, "E185", {"start": v(-15.49, 7.82) * mm, "end": v(-14.24, 7.82) * mm});
            skLineSegment(sketch, "E186", {"start": v(-14.68, 8) * mm, "end": v(-14.68, 8.25) * mm});
            skLineSegment(sketch, "E187", {"start": v(-14.68, 8) * mm, "end": v(-14.24, 8) * mm});
            skLineSegment(sketch, "E188", {"start": v(-14.24, 8) * mm, "end": v(-14.24, 7.82) * mm});
            skLineSegment(sketch, "E189", {"start": v(-14.68, 8.25) * mm, "end": v(-14.98, 8.25) * mm});
            skSolve(sketch);
        }
        {
            var Q0;
            Q0=makeQuery(id+"F5.imprint","IMPRINT",FACE,{"disambiguationData":[TD([[makeQuery(id+"F5.imprint","IMPRINT",EDGE,{"derivedFrom":sQuery(id+"F5.wireOp",EDGE,"E39")}),1.0]])]});
            cPlane(context, id + "F36", {"entities" : qUnion([Q0]), "cplaneType" : CPlaneType.OFFSET, "offset" : 13.65 * mm, "oppositeDirection" : true, "width" : 150 * mm, "height" : 150 * mm});
        }
        {
            var Q0;
            Q0=qCreatedBy(id+"F36.planeOp",FACE);
            var sketch = newSketch(context, id + "F37", { "sketchPlane" : qUnion([Q0])});
            skLineSegment(sketch, "E190.0", {"start": v(31.6, 7.2) * mm, "end": v(31.06, 7.2) * mm});
            skLineSegment(sketch, "E191.0", {"start": v(31.6, 7.2) * mm, "end": v(31.6, 7.75) * mm});
            skLineSegment(sketch, "E192.0", {"start": v(31.06, 7.2) * mm, "end": v(30.56, 6.7) * mm});
            skLineSegment(sketch, "E193.0", {"start": v(30.5, 6.7) * mm, "end": v(30.53, 0.5) * mm});
            skLineSegment(sketch, "E194.0", {"start": v(31.06, 8.25) * mm, "end": v(29, 6.7) * mm});
            skLineSegment(sketch, "E195.0", {"start": v(31.6, 7.75) * mm, "end": v(31.06, 8.25) * mm});
            skLineSegment(sketch, "E196.0", {"start": v(29, 6.7) * mm, "end": v(29, 0.5) * mm});
            skLineSegment(sketch, "E197.0", {"start": v(31.06, -1.15) * mm, "end": v(29, 0.5) * mm});
            skLineSegment(sketch, "E198.0", {"start": v(31.06, 0) * mm, "end": v(31.06, -1.15) * mm});
            skLineSegment(sketch, "E199.0", {"start": v(31.06, 0) * mm, "end": v(30.56, 0.5) * mm});
            skPoint(sketch, "E200.0", {"position": v(59.9, 7.75) * mm});
            skLineSegment(sketch, "E201", {"start": v(59.9, 7.75) * mm, "end": v(59.9, 0) * mm, "construction": true});
            skLineSegment(sketch, "E202.MirrorCS", {"start": v(88.76, 8.25) * mm, "end": v(90.8, 6.7) * mm});
            skLineSegment(sketch, "E203.MirrorCS", {"start": v(88.2, 7.75) * mm, "end": v(88.76, 8.25) * mm});
            skLineSegment(sketch, "E204.MirrorCS", {"start": v(88.2, 7.2) * mm, "end": v(88.2, 7.75) * mm});
            skLineSegment(sketch, "E205.MirrorCS", {"start": v(88.2, 7.2) * mm, "end": v(88.76, 7.2) * mm});
            skLineSegment(sketch, "E206.MirrorCS", {"start": v(88.76, 7.2) * mm, "end": v(89.26, 6.7) * mm});
            skLineSegment(sketch, "E207.MirrorCS", {"start": v(89.3, 6.7) * mm, "end": v(89.28, 0.5) * mm});
            skLineSegment(sketch, "E208.MirrorCS", {"start": v(88.76, -1.15) * mm, "end": v(90.8, 0.5) * mm});
            skLineSegment(sketch, "E209.MirrorCS", {"start": v(88.76, 0) * mm, "end": v(89.26, 0.5) * mm});
            skLineSegment(sketch, "E210.MirrorCS", {"start": v(88.76, 0) * mm, "end": v(88.76, -1.15) * mm});
            skLineSegment(sketch, "E211", {"start": v(90.8, 6.7) * mm, "end": v(89.6, 6.7) * mm});
            skLineSegment(sketch, "E212", {"start": v(89.6, 6.7) * mm, "end": v(88.2, 7.75) * mm});
            skSolve(sketch);
        }
        {
            var Q0;
            Q0=makeQuery(id+"F23.opSweep","SWEPT_FACE",FACE,{"disambiguationData":[OSD([sQuery(id+"F21.wireOp",EDGE,"E117"),sQuery(id+"F22.wireOp",EDGE,"E125.0")])]});
            var sketch = newSketch(context, id + "F38", { "sketchPlane" : qUnion([Q0])});
            skPoint(sketch, "E213.0", {"position": v(13.65, 6.7) * mm});
            skLineSegment(sketch, "E214", {"start": v(13.65, 6.7) * mm, "end": v(13.65, 0.5) * mm});
            skSolve(sketch);
        }
        {
            var Q0;
            {var subQ0=sQuery(id+"F3.wireOp",EDGE,"E14");Q0=makeQuery(id+"F3.imprint","IMPRINT",FACE,{"disambiguationData":[TD([[makeQuery(id+"F3.imprint","IMPRINT",EDGE,{"derivedFrom":subQ0}),-1.0]])]});}
            var sketch = newSketch(context, id + "F39", { "sketchPlane" : qUnion([Q0])});
            skArc(sketch, "E215.0", {"start": v(88.76, -8.15) * mm, "mid": v(86.52, -2.74) * mm, "end": v(81.1, -0.5) * mm});
            skLineSegment(sketch, "E216.0", {"start": v(88.76, -115.85) * mm, "end": v(88.76, -8.15) * mm});
            skLineSegment(sketch, "E217.0", {"start": v(81.1, -0.5) * mm, "end": v(38.7, -0.5) * mm});
            skArc(sketch, "E218.0", {"start": v(38.7, -0.5) * mm, "mid": v(33.3, -2.74) * mm, "end": v(31.06, -8.15) * mm});
            skLineSegment(sketch, "E219.0", {"start": v(31.06, -8.15) * mm, "end": v(31.06, -115.85) * mm});
            skArc(sketch, "E220.0", {"start": v(31.06, -115.85) * mm, "mid": v(33.3, -121.26) * mm, "end": v(38.7, -123.5) * mm});
            skLineSegment(sketch, "E221.0", {"start": v(38.7, -123.5) * mm, "end": v(81.1, -123.5) * mm});
            skArc(sketch, "E222.0", {"start": v(81.1, -123.5) * mm, "mid": v(86.52, -121.26) * mm, "end": v(88.76, -115.85) * mm});
            skSolve(sketch);
        }
        {
            var Q0;
            Q0 = qSketchRegion(id + "F39", true);
            extrude(context, id + "F40", {"entities" : qUnion([Q0]), "operationType" : NewBodyOperationType.ADD, "depth" : 1.15 * mm});
        }
        {
            var Q0;
            Q0=makeQuery(id+"F40.opExtrude","CAP_FACE",FACE,{"disambiguationData":[OSD([sQuery(id+"F39.wireOp",EDGE,"E215.0"),sQuery(id+"F39.wireOp",EDGE,"E216.0"),sQuery(id+"F39.wireOp",EDGE,"E217.0"),sQuery(id+"F39.wireOp",EDGE,"E218.0"),sQuery(id+"F39.wireOp",EDGE,"E219.0"),sQuery(id+"F39.wireOp",EDGE,"E220.0"),sQuery(id+"F39.wireOp",EDGE,"E221.0"),sQuery(id+"F39.wireOp",EDGE,"E222.0")])],"isStart":false});
            var sketch = newSketch(context, id + "F41", { "sketchPlane" : qUnion([Q0])});
            skFitSpline(sketch, "E223.0", {"points": [v(88.76, -8.5) * mm, v(88.76, -44.28) * mm, v(88.76, -80.07) * mm, v(88.76, -115.85) * mm]});
            skPoint(sketch, "E224.0", {"position": v(89.26, -13.65) * mm});
            skPoint(sketch, "E225", {"position": v(88.76, -13.65) * mm});
            skLineSegment(sketch, "E226", {"start": v(88.76, -13.65) * mm, "end": v(31.76, -13.65) * mm});
            skSolve(sketch);
        }
        {
            var Q0;
            Q0 = qSketchRegion(id + "F35", true);
            var Q1;
            Q1=makeQuery(id+"F31.opExtrude","CAP_EDGE",EDGE,{"disambiguationData":[OSD([sQuery(id+"F30.wireOp",EDGE,"E176")])],"isStart":false});
            var Q2;
            Q2=sQuery(id+"F37.wireOp",EDGE,"E202.MirrorCS");
            var Q3;
            Q3=sQuery(id+"F38.wireOp",EDGE,"E214");
            var Q4;
            Q4=sQuery(id+"F37.wireOp",EDGE,"E208.MirrorCS");
            var Q5;
            Q5=sQuery(id+"F41.wireOp",EDGE,"E226");
            sweep(context, id + "F42", {"operationType" : NewBodyOperationType.REMOVE, "profiles" : qUnion([Q0]), "path" : qUnion([Q1, Q2, Q3, Q4, Q5])});
        }
        {
            var Q0;
            Q0=makeQuery(id+"F23.opSweep","SWEPT_FACE",FACE,{"disambiguationData":[OSD([sQuery(id+"F21.wireOp",EDGE,"E117"),sQuery(id+"F22.wireOp",EDGE,"E123.0")])]});
            var sketch = newSketch(context, id + "F43", { "sketchPlane" : qUnion([Q0])});
            skCircle(sketch, "E227", {"center": v(-78.5, 3.88) * mm, "radius": 1.5 * mm});
            skCircle(sketch, "E228", {"center": v(-70.66, 3.88) * mm, "radius": 1.5 * mm});
            skLineSegment(sketch, "E229", {"start": v(-78.5, 5.38) * mm, "end": v(-70.66, 5.38) * mm});
            skLineSegment(sketch, "E230", {"start": v(-70.66, 2.38) * mm, "end": v(-78.5, 2.38) * mm});
            skSolve(sketch);
        }
        {
            var Q0;
            Q0 = qSketchRegion(id + "F43", true);
            extrude(context, id + "F44", {"entities" : qUnion([Q0]), "operationType" : NewBodyOperationType.REMOVE, "oppositeDirection" : true, "depth" : 5 * mm});
        }
    });
